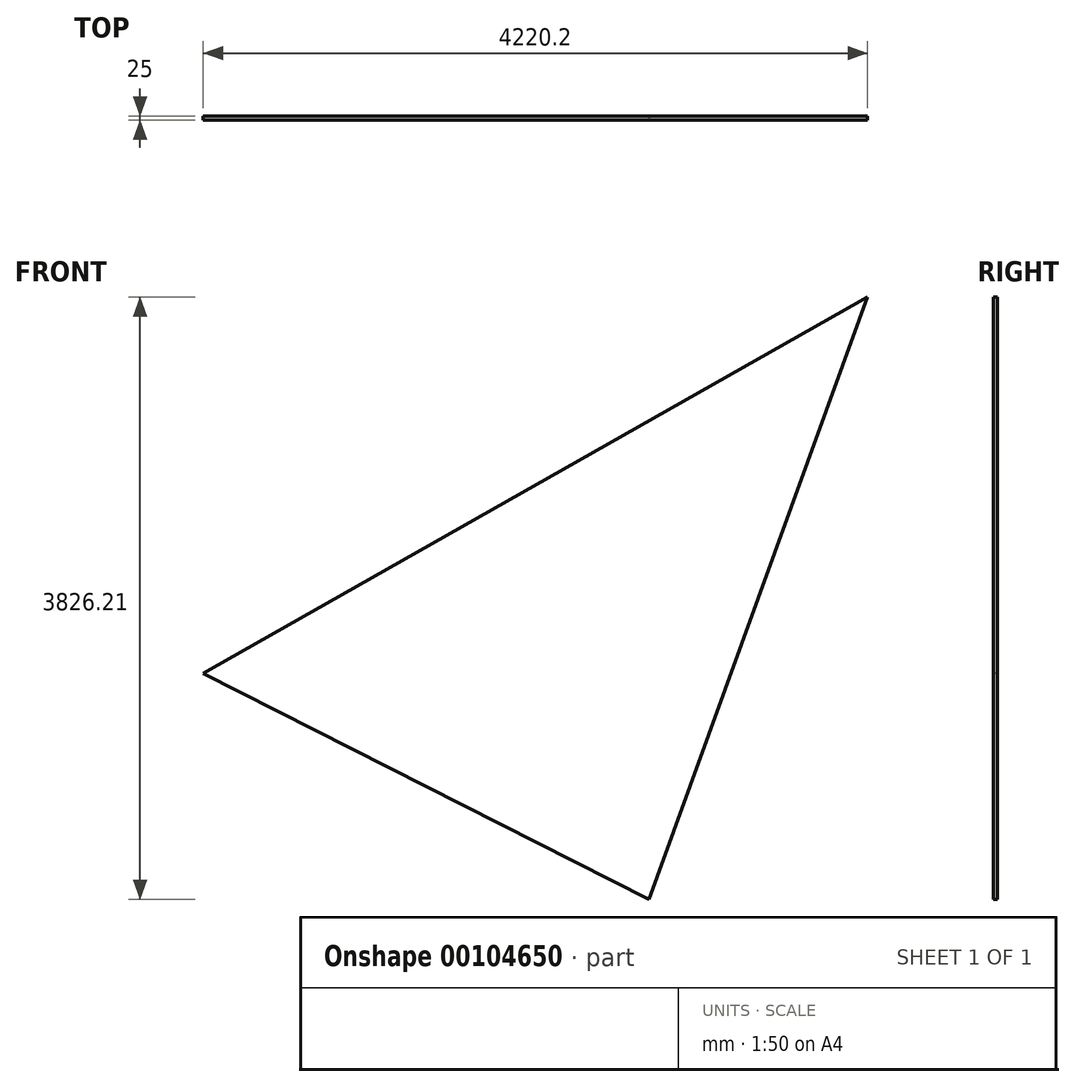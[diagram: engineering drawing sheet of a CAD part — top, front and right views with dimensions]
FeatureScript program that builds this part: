
annotation { "Feature Type Name" : "Feature", "Feature Type Description" : "" }
export const myFeature = defineFeature(function(context is Context, id is Id, definition is map)
    precondition{}
    {
        {
            var Q0;
            Q0=qCreatedBy(makeId("Front.planeOp"),FACE);
            var sketch = newSketch(context, id + "F0", { "sketchPlane" : qUnion([Q0])});
            skLineSegment(sketch, "E0", {"start": v(0, 0) * mm, "end": v(2832.75, -1436.15) * mm});
            skLineSegment(sketch, "E1", {"start": v(2832.75, -1436.15) * mm, "end": v(4220.2, 2390.06) * mm});
            skLineSegment(sketch, "E2", {"start": v(4220.2, 2390.06) * mm, "end": v(0, 0) * mm});
            skSolve(sketch);
        }
        {
            var Q0;
            Q0=makeQuery(id+"F0.imprint","IMPRINT",FACE,{"disambiguationData":[TD([[makeQuery(id+"F0.imprint","IMPRINT",EDGE,{"derivedFrom":sQuery(id+"F0.wireOp",EDGE,"E0")}),1.0]])]});
            extrude(context, id + "F1", {"entities" : qUnion([Q0]), "oppositeDirection" : true, "depth" : 25 * mm});
        }
    });
